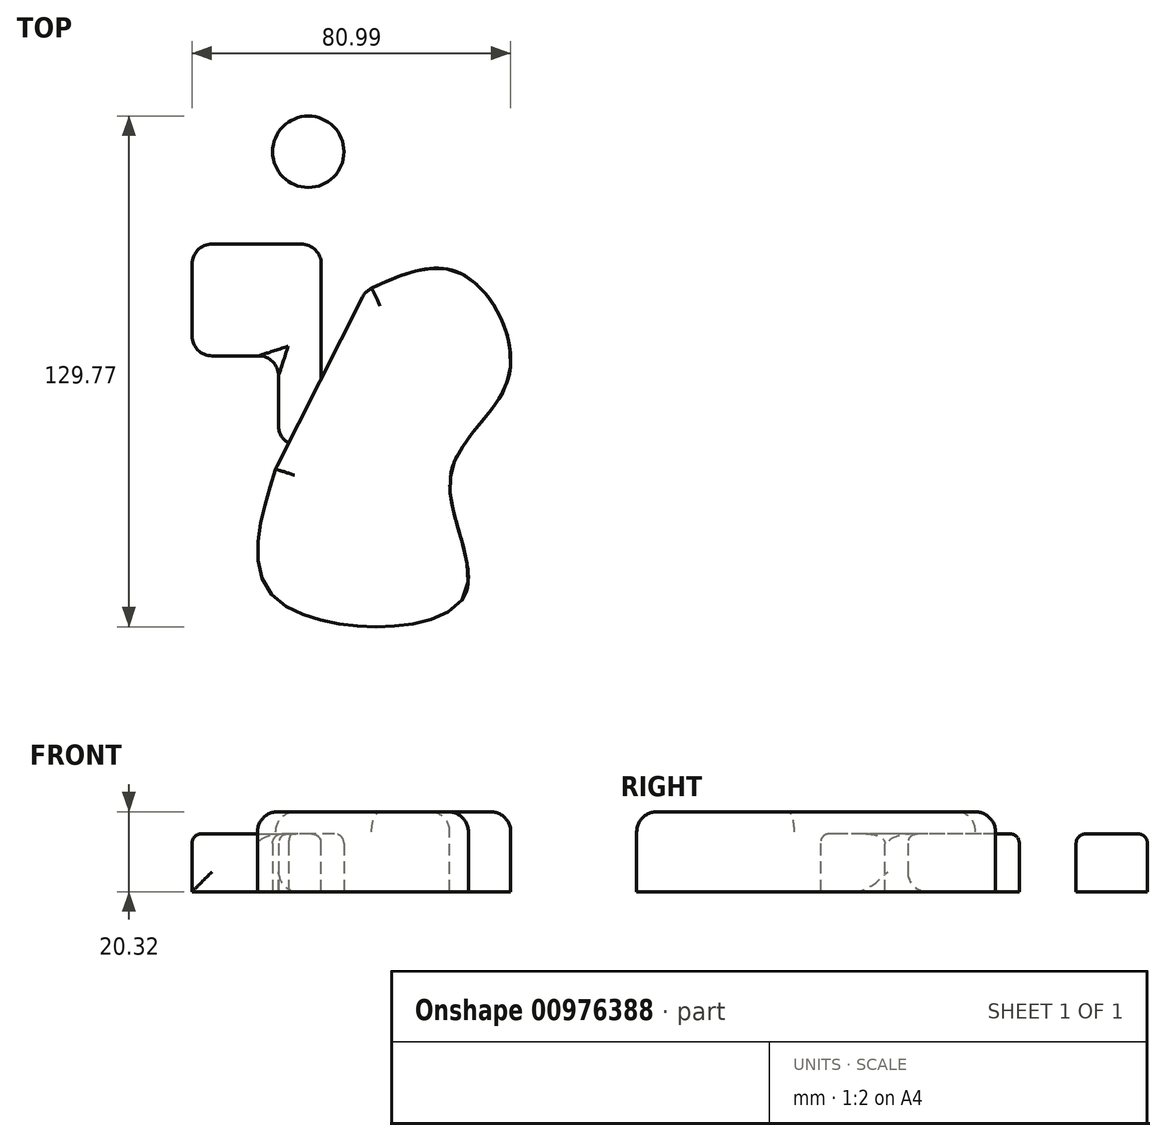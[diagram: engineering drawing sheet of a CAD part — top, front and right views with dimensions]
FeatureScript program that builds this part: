
annotation { "Feature Type Name" : "Feature", "Feature Type Description" : "" }
export const myFeature = defineFeature(function(context is Context, id is Id, definition is map)
    precondition{}
    {
        {
            var Q0;
            Q0=qCreatedBy(makeId("Top.planeOp"),FACE);
            var sketch = newSketch(context, id + "F0", { "sketchPlane" : qUnion([Q0])});
            skLineSegment(sketch, "E0.bottom", {"start": v(-62.8, 0) * mm, "end": v(-29.95, 0) * mm});
            skLineSegment(sketch, "E0.top", {"start": v(-62.8, -28.37) * mm, "end": v(-29.95, -28.37) * mm});
            skLineSegment(sketch, "E0.left", {"start": v(-62.8, 0) * mm, "end": v(-62.8, -28.37) * mm});
            skLineSegment(sketch, "E0.right", {"start": v(-29.95, 0) * mm, "end": v(-29.95, -28.37) * mm});
            skLineSegment(sketch, "E1.bottom", {"start": v(-40.8, -28.37) * mm, "end": v(-29.95, -28.37) * mm});
            skLineSegment(sketch, "E1.top", {"start": v(-40.8, -51.22) * mm, "end": v(-29.95, -51.22) * mm});
            skLineSegment(sketch, "E1.left", {"start": v(-40.8, -28.37) * mm, "end": v(-40.8, -51.22) * mm});
            skLineSegment(sketch, "E1.right", {"start": v(-29.95, -28.37) * mm, "end": v(-29.95, -51.22) * mm});
            skCircle(sketch, "E2", {"center": v(-33.24, 23.48) * mm, "radius": 9.07 * mm});
            skSolve(sketch);
        }
        {
            var Q0;
            Q0=makeQuery(id+"F0.imprint","IMPRINT",FACE,{"disambiguationData":[TD([[makeQuery(id+"F0.imprint","IMPRINT",EDGE,{"derivedFrom":sQuery(id+"F0.wireOp",EDGE,"E0.bottom")}),-1.0]])]});
            var Q1;
            Q1=makeQuery(id+"F0.imprint","IMPRINT",FACE,{"disambiguationData":[TD([[makeQuery(id+"F0.imprint","IMPRINT",EDGE,{"derivedFrom":sQuery(id+"F0.wireOp",EDGE,"E1.top")}),1.0]])]});
            var Q2;
            Q2=makeQuery(id+"F0.imprint","IMPRINT",FACE,{"disambiguationData":[TD([[makeQuery(id+"F0.imprint","IMPRINT",EDGE,{"derivedFrom":sQuery(id+"F0.wireOp",EDGE,"E2")}),1.0]])]});
            extrude(context, id + "F1", {"entities" : qUnion([Q0, Q1, Q2]), "depth" : 14.73 * mm, "offsetDistance" : 25.4 * mm});
        }
        {
            var Q0;
            Q0=makeQuery(id+"F1.opExtrude","CAP_FACE",FACE,{"disambiguationData":[OSD([sQuery(id+"F0.wireOp",EDGE,"E2")])],"isStart":false});
            extrude(context, id + "F2", {"entities" : qUnion([Q0]), "operationType" : NewBodyOperationType.ADD, "oppositeDirection" : true, "depth" : 7.37 * mm, "offsetDistance" : 25.4 * mm});
        }
        {
            var Q0;
            Q0=makeQuery(id+"F1.opExtrude","CAP_EDGE",EDGE,{"disambiguationData":[OSD([sQuery(id+"F0.wireOp",EDGE,"E0.right"),sQuery(id+"F0.wireOp",EDGE,"E1.right")])],"isStart":false});
            var Q1;
            Q1=makeQuery(id+"F1.opExtrude","CAP_EDGE",EDGE,{"disambiguationData":[OSD([sQuery(id+"F0.wireOp",EDGE,"E1.top")])],"isStart":false});
            var Q2;
            Q2=makeQuery(id+"F1.opExtrude","CAP_EDGE",EDGE,{"disambiguationData":[OSD([sQuery(id+"F0.wireOp",EDGE,"E1.left")])],"isStart":false});
            var Q3;
            Q3=makeQuery(id+"F1.opExtrude","CAP_EDGE",EDGE,{"disambiguationData":[OSD([sQuery(id+"F0.wireOp",EDGE,"E0.top")])],"isStart":false});
            var Q4;
            Q4=makeQuery(id+"F1.opExtrude","CAP_EDGE",EDGE,{"disambiguationData":[OSD([sQuery(id+"F0.wireOp",EDGE,"E0.left")])],"isStart":false});
            var Q5;
            Q5=makeQuery(id+"F1.opExtrude","CAP_EDGE",EDGE,{"disambiguationData":[OSD([sQuery(id+"F0.wireOp",EDGE,"E0.bottom")])],"isStart":false});
            var Q6;
            Q6=makeQuery(id+"F1.opExtrude","CAP_EDGE",EDGE,{"disambiguationData":[OSD([sQuery(id+"F0.wireOp",EDGE,"E2")])],"isStart":false});
            fillet(context, id + "F3", {"entities" : qUnion([Q0, Q1, Q2, Q3, Q4, Q5, Q6]), "radius" : 2.45 * mm, "tangentPropagation" : true, "allowEdgeOverflow" : false});
        }
        {
            var Q0;
            Q0=makeQuery(id+"F1.opExtrude","SWEPT_EDGE",EDGE,{"disambiguationData":[OSD([sQuery(id+"F0.wireOp",EDGE,"E1.top"),sQuery(id+"F0.wireOp",EDGE,"E1.right")])]});
            var Q1;
            Q1=makeQuery(id+"F1.opExtrude","SWEPT_EDGE",EDGE,{"disambiguationData":[OSD([sQuery(id+"F0.wireOp",EDGE,"E1.top"),sQuery(id+"F0.wireOp",EDGE,"E1.left")])]});
            var Q2;
            Q2=makeQuery(id+"F1.opExtrude","SWEPT_FACE",FACE,{"disambiguationData":[OSD([sQuery(id+"F0.wireOp",EDGE,"E0.top")])]});
            var Q3;
            Q3=makeQuery(id+"F1.opExtrude","SWEPT_EDGE",EDGE,{"disambiguationData":[OSD([sQuery(id+"F0.wireOp",EDGE,"E0.bottom"),sQuery(id+"F0.wireOp",EDGE,"E0.right")])]});
            var Q4;
            Q4=makeQuery(id+"F3.opFillet","BLEND_EDGE",EDGE,{"blendedFrom":[makeQuery(id+"F1.opExtrude","CAP_EDGE",EDGE,{"disambiguationData":[OSD([sQuery(id+"F0.wireOp",EDGE,"E0.bottom")])],"isStart":false}),makeQuery(id+"F1.opExtrude","CAP_EDGE",EDGE,{"disambiguationData":[OSD([sQuery(id+"F0.wireOp",EDGE,"E0.left")])],"isStart":false})],"blendedInto":[]});
            fillet(context, id + "F4", {"entities" : qUnion([Q0, Q1, Q2, Q3, Q4]), "radius" : 5.08 * mm, "tangentPropagation" : true, "allowEdgeOverflow" : false});
        }
        {
            var Q0;
            Q0=qCreatedBy(makeId("Top.planeOp"),FACE);
            var sketch = newSketch(context, id + "F5", { "sketchPlane" : qUnion([Q0])});
            skCircle(sketch, "E3.cCircle", {"center": v(-9.64, -35.62) * mm, "radius": 13.09 * mm, "construction": true});
            skLineSegment(sketch, "E3.0", {"start": v(-13.33, -50.28) * mm, "end": v(-24.17, -39.76) * mm});
            skLineSegment(sketch, "E3.1", {"start": v(-24.17, -39.76) * mm, "end": v(-20.48, -25.1) * mm});
            skLineSegment(sketch, "E3.2", {"start": v(-20.48, -25.1) * mm, "end": v(-5.95, -20.97) * mm});
            skLineSegment(sketch, "E3.3", {"start": v(-5.95, -20.97) * mm, "end": v(4.9, -31.5) * mm});
            skLineSegment(sketch, "E3.4", {"start": v(4.9, -31.5) * mm, "end": v(1.21, -46.15) * mm});
            skLineSegment(sketch, "E3.5", {"start": v(1.21, -46.15) * mm, "end": v(-13.33, -50.28) * mm});
            skPoint(sketch, "E3.0.midPoint", {"position": v(-18.75, -45.02) * mm});
            skFitSpline(sketch, "E4", {"points": [v(-18.72, -11.93) * mm, v(5.58, -7.46) * mm, v(17.73, -33.44) * mm, v(2.8, -59.23) * mm, v(5.7, -90.56) * mm, v(-40.72, -90.69) * mm, v(-41.38, -56.77) * mm], "startDerivative": vector(174.38, 82.58) * mm, "endDerivative": vector(74.35, 233.19) * mm});
            skFitSpline(sketch, "E5", {"points": [v(-41.38, -56.77) * mm, v(-18.72, -11.93) * mm], "startDerivative": vector(22.67, 44.84) * mm, "endDerivative": vector(22.67, 44.84) * mm});
            skSolve(sketch);
        }
        {
            var Q0;
            Q0=makeQuery(id+"F5.imprint","IMPRINT",FACE,{"disambiguationData":[TD([[makeQuery(id+"F5.imprint","IMPRINT",EDGE,{"derivedFrom":sQuery(id+"F5.wireOp",EDGE,"E3.0")}),-1.0]])]});
            var Q1;
            Q1=makeQuery(id+"F5.imprint","IMPRINT",FACE,{"disambiguationData":[TD([[makeQuery(id+"F5.imprint","IMPRINT",EDGE,{"derivedFrom":sQuery(id+"F5.wireOp",EDGE,"E3.0")}),1.0]])]});
            extrude(context, id + "F6", {"entities" : qUnion([Q0, Q1]), "operationType" : NewBodyOperationType.ADD, "depth" : 20.32 * mm, "offsetDistance" : 25.4 * mm});
        }
        {
            var Q0;
            Q0=makeQuery(id+"F6.opExtrude","CAP_EDGE",EDGE,{"disambiguationData":[OSD([sQuery(id+"F5.wireOp",EDGE,"E4")])],"isStart":false});
            fillet(context, id + "F7", {"entities" : qUnion([Q0]), "radius" : 5.08 * mm, "tangentPropagation" : true, "allowEdgeOverflow" : false});
        }
        {
            var Q0;
            Q0=makeQuery(id+"F6.opExtrude","CAP_EDGE",EDGE,{"disambiguationData":[OSD([sQuery(id+"F5.wireOp",EDGE,"E5")])],"isStart":false});
            var Q1;
            Q1=makeQuery(id+"F7.opFillet","BLEND_EDGE",EDGE,{"disambiguationData":[OD(1.0)],"blendedFrom":[makeQuery(id+"F6.opExtrude","CAP_EDGE",EDGE,{"disambiguationData":[OSD([sQuery(id+"F5.wireOp",EDGE,"E4")])],"isStart":false}),makeQuery(id+"F6.opExtrude","SWEPT_FACE",FACE,{"disambiguationData":[OSD([sQuery(id+"F5.wireOp",EDGE,"E5")])]})],"blendedInto":[makeQuery(id+"F6.opExtrude","SWEPT_FACE",FACE,{"disambiguationData":[OSD([sQuery(id+"F5.wireOp",EDGE,"E5")])]})]});
            fillet(context, id + "F8", {"entities" : qUnion([Q0, Q1]), "radius" : 5.08 * mm, "tangentPropagation" : true, "allowEdgeOverflow" : false});
        }
    });
